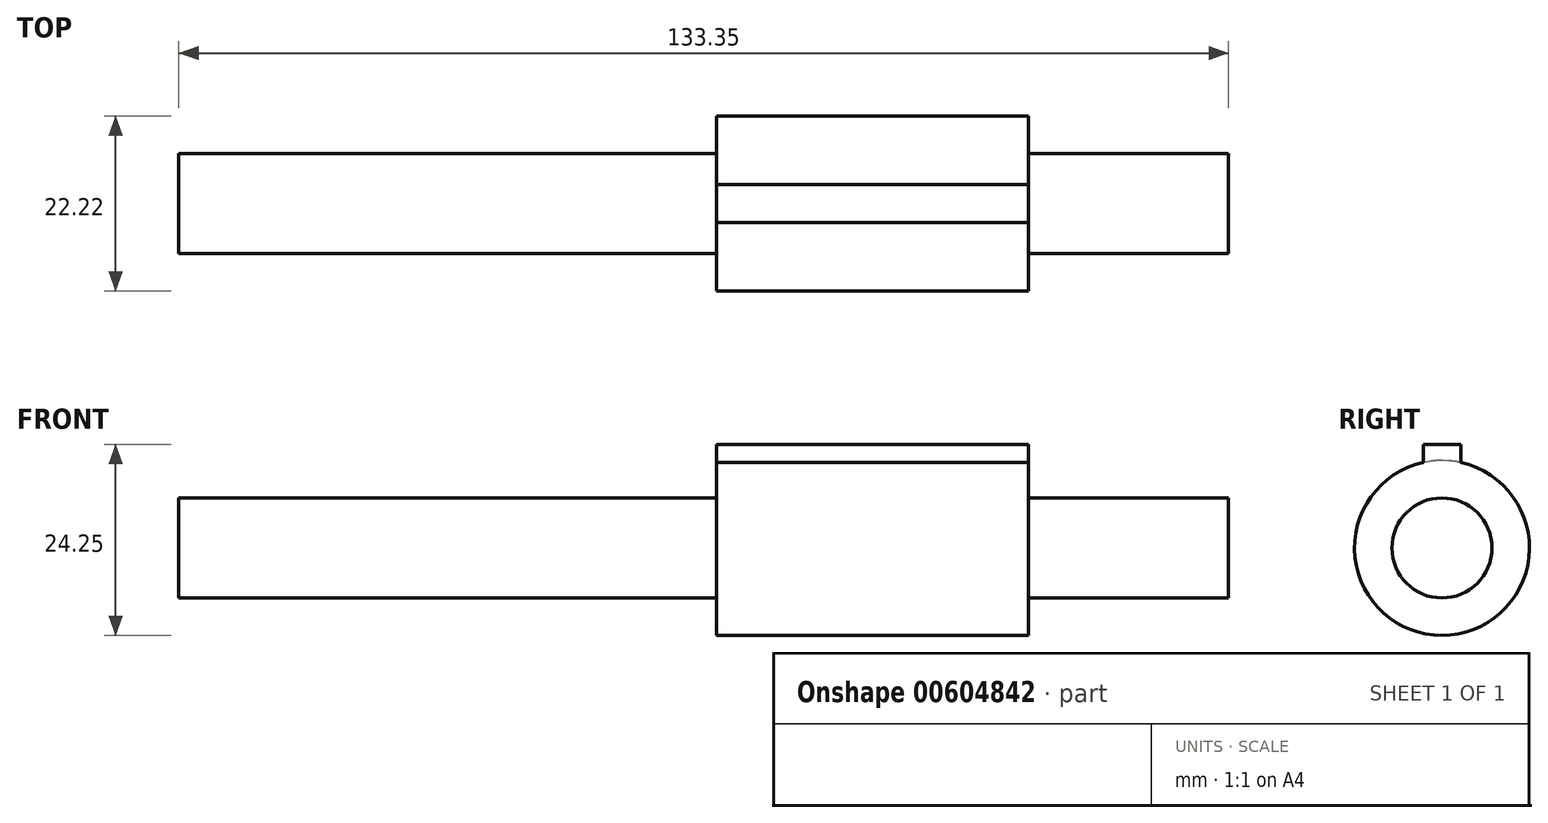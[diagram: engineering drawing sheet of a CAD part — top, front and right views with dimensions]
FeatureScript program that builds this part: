
annotation { "Feature Type Name" : "Feature", "Feature Type Description" : "" }
export const myFeature = defineFeature(function(context is Context, id is Id, definition is map)
    precondition{}
    {
        {
            var Q0;
            Q0=qCreatedBy(makeId("Front.planeOp"),FACE);
            var sketch = newSketch(context, id + "F0", { "sketchPlane" : qUnion([Q0])});
            skLineSegment(sketch, "E0.bottom", {"start": v(0, 0) * mm, "end": v(133.35, 0) * mm});
            skLineSegment(sketch, "E0.left", {"start": v(0, 0) * mm, "end": v(0, 6.35) * mm});
            skLineSegment(sketch, "E0.right", {"start": v(133.35, 0) * mm, "end": v(133.35, 6.35) * mm});
            skLineSegment(sketch, "E1.top", {"start": v(120.65, 11.11) * mm, "end": v(80.98, 11.11) * mm});
            skLineSegment(sketch, "E1.left", {"start": v(120.65, 6.35) * mm, "end": v(120.65, 11.11) * mm});
            skLineSegment(sketch, "E1.right", {"start": v(80.98, 6.35) * mm, "end": v(80.98, 11.11) * mm});
            skLineSegment(sketch, "E2", {"start": v(80.98, 6.35) * mm, "end": v(0, 6.35) * mm});
            skLineSegment(sketch, "E3", {"start": v(120.65, 6.35) * mm, "end": v(133.35, 6.35) * mm});
            skSolve(sketch);
        }
        {
            var Q0;
            Q0 = qSketchRegion(id + "F0", true);
            var Q1;
            Q1=sQuery(id+"F0.wireOp",EDGE,"E0.bottom");
            revolve(context, id + "F1", {"entities" : qUnion([Q0]), "axis" : qUnion([Q1]), "revolveType" : RevolveType.FULL});
        }
        {
            var Q0;
            Q0=makeQuery(id+"F1.opRevolve","SWEPT_FACE",FACE,{"disambiguationData":[OSD([sQuery(id+"F0.wireOp",EDGE,"E1.left")])]});
            var sketch = newSketch(context, id + "F2", { "sketchPlane" : qUnion([Q0])});
            skLineSegment(sketch, "E4", {"start": v(-2.39, 10.85) * mm, "end": v(2.39, 10.85) * mm});
            skLineSegment(sketch, "E5", {"start": v(-2.39, 10.85) * mm, "end": v(-2.39, 13.14) * mm});
            skLineSegment(sketch, "E6", {"start": v(2.39, 10.85) * mm, "end": v(2.39, 13.14) * mm});
            skLineSegment(sketch, "E7", {"start": v(2.39, 13.14) * mm, "end": v(-2.39, 13.14) * mm});
            skSolve(sketch);
        }
        {
            var Q0;
            {var subQ0=sQuery(id+"F2.wireOp",EDGE,"E5");Q0=makeQuery(id+"F2.imprint","IMPRINT",FACE,{"disambiguationData":[TD([[makeQuery(id+"F2.imprint","IMPRINT",EDGE,{"derivedFrom":subQ0}),-1.0]])]});}
            extrude(context, id + "F3", {"entities" : qUnion([Q0]), "operationType" : NewBodyOperationType.ADD, "oppositeDirection" : true, "depth" : 39.65 * mm, "offsetDistance" : 25 * mm});
        }
        {
            var Q0;
            Q0=makeQuery(id+"F1.opRevolve","SWEPT_FACE",FACE,{"disambiguationData":[OSD([sQuery(id+"F0.wireOp",EDGE,"E0.right")])]});
            extrude(context, id + "F4", {"entities" : qUnion([Q0]), "operationType" : NewBodyOperationType.ADD, "depth" : 12.7 * mm, "offsetDistance" : 25 * mm});
        }
        {
            var Q0;
            Q0=makeQuery(id+"F1.opRevolve","SWEPT_FACE",FACE,{"disambiguationData":[OSD([sQuery(id+"F0.wireOp",EDGE,"E0.left")])]});
            extrude(context, id + "F5", {"entities" : qUnion([Q0]), "operationType" : NewBodyOperationType.REMOVE, "oppositeDirection" : true, "depth" : 12.7 * mm, "offsetDistance" : 25 * mm});
        }
    });
